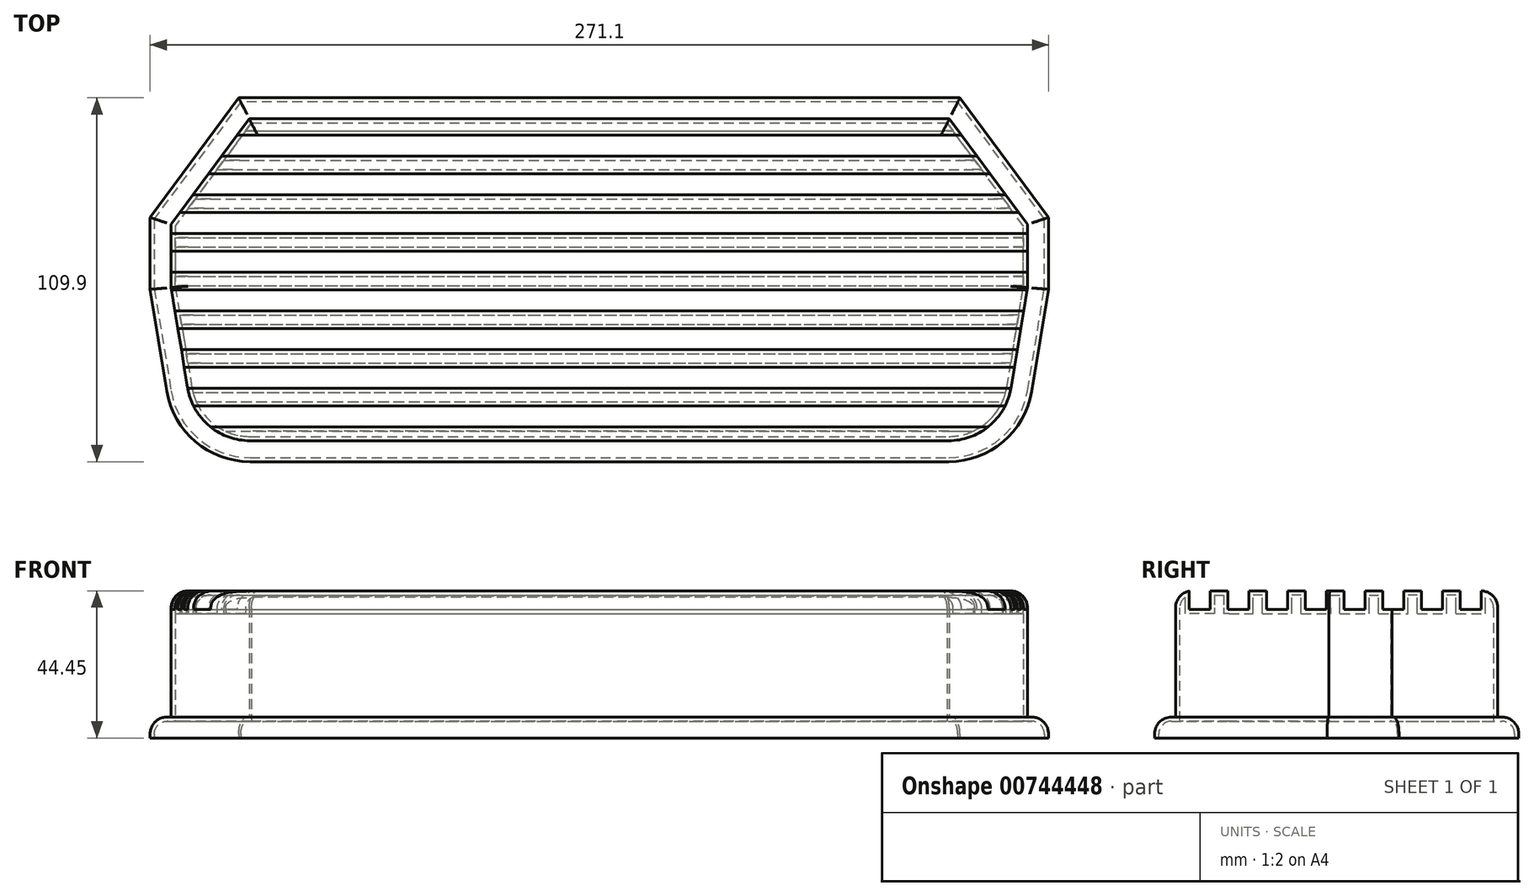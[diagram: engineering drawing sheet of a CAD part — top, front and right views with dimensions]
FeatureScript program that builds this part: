
annotation { "Feature Type Name" : "Feature", "Feature Type Description" : "" }
export const myFeature = defineFeature(function(context is Context, id is Id, definition is map)
    precondition{}
    {
        {
            var Q0;
            Q0=qCreatedBy(makeId("Top.planeOp"),FACE);
            var sketch = newSketch(context, id + "F0", { "sketchPlane" : qUnion([Q0])});
            skLineSegment(sketch, "E0.0.0", {"start": v(-203.12, -79.65) * mm, "end": v(7.7, -79.65) * mm});
            skArc(sketch, "E0.0.1", {"start": v(7.7, -79.65) * mm, "mid": v(20.03, -75.13) * mm, "end": v(26.5, -63.7) * mm});
            skLineSegment(sketch, "E0.0.2", {"start": v(26.5, -63.7) * mm, "end": v(31.49, -33.42) * mm});
            skLineSegment(sketch, "E0.0.3", {"start": v(31.49, -33.42) * mm, "end": v(31.49, -14.33) * mm});
            skLineSegment(sketch, "E0.0.4", {"start": v(31.49, -14.33) * mm, "end": v(7.9, 17.55) * mm});
            skLineSegment(sketch, "E0.0.5", {"start": v(7.9, 17.55) * mm, "end": v(-203.33, 17.55) * mm});
            skLineSegment(sketch, "E0.0.6", {"start": v(-203.33, 17.55) * mm, "end": v(-226.91, -14.33) * mm});
            skLineSegment(sketch, "E0.0.7", {"start": v(-226.91, -14.33) * mm, "end": v(-226.91, -33.42) * mm});
            skLineSegment(sketch, "E0.0.8", {"start": v(-226.91, -33.42) * mm, "end": v(-221.92, -63.7) * mm});
            skArc(sketch, "E0.0.9", {"start": v(-221.92, -63.7) * mm, "mid": v(-215.45, -75.13) * mm, "end": v(-203.12, -79.65) * mm});
            skArc(sketch, "E1.0", {"start": v(-228.19, -64.73) * mm, "mid": v(-219.56, -79.97) * mm, "end": v(-203.12, -86) * mm});
            skLineSegment(sketch, "E1.1", {"start": v(-233.26, -33.94) * mm, "end": v(-228.19, -64.73) * mm});
            skLineSegment(sketch, "E1.2", {"start": v(-203.12, -86) * mm, "end": v(7.7, -86) * mm});
            skLineSegment(sketch, "E1.3", {"start": v(-233.26, -12.24) * mm, "end": v(-233.26, -33.94) * mm});
            skLineSegment(sketch, "E1.4", {"start": v(-206.53, 23.9) * mm, "end": v(-233.26, -12.24) * mm});
            skLineSegment(sketch, "E1.5", {"start": v(11.1, 23.9) * mm, "end": v(-206.53, 23.9) * mm});
            skArc(sketch, "E1.6", {"start": v(7.7, -86) * mm, "mid": v(24.14, -79.97) * mm, "end": v(32.76, -64.73) * mm});
            skLineSegment(sketch, "E1.7", {"start": v(32.76, -64.73) * mm, "end": v(37.84, -33.94) * mm});
            skLineSegment(sketch, "E1.8", {"start": v(37.84, -33.94) * mm, "end": v(37.84, -12.24) * mm});
            skLineSegment(sketch, "E1.9", {"start": v(37.84, -12.24) * mm, "end": v(11.1, 23.9) * mm});
            skSolve(sketch);
        }
        {
            var Q0;
            Q0=makeQuery(id+"F0.imprint","IMPRINT",FACE,{"disambiguationData":[TD([[makeQuery(id+"F0.imprint","IMPRINT",EDGE,{"derivedFrom":sQuery(id+"F0.wireOp",EDGE,"E0.0.0")}),1.0]])]});
            extrude(context, id + "F1", {"entities" : qUnion([Q0]), "depth" : 44.45 * mm});
        }
        {
            var Q0;
            Q0=makeQuery(id+"F0.imprint","IMPRINT",FACE,{"disambiguationData":[TD([[makeQuery(id+"F0.imprint","IMPRINT",EDGE,{"derivedFrom":sQuery(id+"F0.wireOp",EDGE,"E0.0.0")}),-1.0]])]});
            extrude(context, id + "F2", {"entities" : qUnion([Q0]), "operationType" : NewBodyOperationType.ADD, "depth" : 6.35 * mm});
        }
        {
            var Q0;
            Q0=makeQuery(id+"F1.opExtrude","CAP_FACE",FACE,{"disambiguationData":[OSD([sQuery(id+"F0.wireOp",EDGE,"E0.0.0"),sQuery(id+"F0.wireOp",EDGE,"E0.0.1"),sQuery(id+"F0.wireOp",EDGE,"E0.0.2"),sQuery(id+"F0.wireOp",EDGE,"E0.0.3"),sQuery(id+"F0.wireOp",EDGE,"E0.0.4"),sQuery(id+"F0.wireOp",EDGE,"E0.0.5"),sQuery(id+"F0.wireOp",EDGE,"E0.0.6"),sQuery(id+"F0.wireOp",EDGE,"E0.0.7"),sQuery(id+"F0.wireOp",EDGE,"E0.0.8"),sQuery(id+"F0.wireOp",EDGE,"E0.0.9")])],"isStart":false});
            var Q1;
            Q1=makeQuery(id+"F2.opExtrude","CAP_EDGE",EDGE,{"disambiguationData":[OSD([sQuery(id+"F0.wireOp",EDGE,"E1.4")])],"isStart":false});
            var Q2;
            Q2=makeQuery(id+"F2.opExtrude","CAP_EDGE",EDGE,{"disambiguationData":[OSD([sQuery(id+"F0.wireOp",EDGE,"E1.3")])],"isStart":false});
            var Q3;
            Q3=makeQuery(id+"F2.opExtrude","CAP_EDGE",EDGE,{"disambiguationData":[OSD([sQuery(id+"F0.wireOp",EDGE,"E1.1")])],"isStart":false});
            var Q4;
            Q4=makeQuery(id+"F2.opExtrude","CAP_EDGE",EDGE,{"disambiguationData":[OSD([sQuery(id+"F0.wireOp",EDGE,"E1.5")])],"isStart":false});
            var Q5;
            Q5=makeQuery(id+"F2.opExtrude","CAP_EDGE",EDGE,{"disambiguationData":[OSD([sQuery(id+"F0.wireOp",EDGE,"E1.8")])],"isStart":false});
            var Q6;
            Q6=makeQuery(id+"F2.opExtrude","CAP_EDGE",EDGE,{"disambiguationData":[OSD([sQuery(id+"F0.wireOp",EDGE,"E1.9")])],"isStart":false});
            fillet(context, id + "F3", {"entities" : qUnion([Q0, Q1, Q2, Q3, Q4, Q5, Q6]), "radius" : 5.08 * mm, "tangentPropagation" : true, "allowEdgeOverflow" : false});
        }
        {
            var Q0;
            Q0=qCreatedBy(makeId("Right.planeOp"),FACE);
            var sketch = newSketch(context, id + "F4", { "sketchPlane" : qUnion([Q0])});
            skLineSegment(sketch, "E2.bottom", {"start": v(12.62, 51.56) * mm, "end": v(6.27, 51.56) * mm});
            skLineSegment(sketch, "E2.top", {"start": v(12.62, 38.86) * mm, "end": v(6.27, 38.86) * mm});
            skLineSegment(sketch, "E2.left", {"start": v(12.62, 51.56) * mm, "end": v(12.62, 38.86) * mm});
            skLineSegment(sketch, "E2.right", {"start": v(6.27, 51.56) * mm, "end": v(6.27, 38.86) * mm});
            skPoint(sketch, "E2.middle", {"position": v(9.45, 45.2) * mm});
            skLineSegment(sketch, "E3.1.0.0", {"start": v(-5.4, 51.56) * mm, "end": v(-5.4, 38.86) * mm});
            skLineSegment(sketch, "E3.1.0.1", {"start": v(0.94, 51.56) * mm, "end": v(-5.4, 51.56) * mm});
            skLineSegment(sketch, "E3.1.0.2", {"start": v(0.94, 51.56) * mm, "end": v(0.94, 38.86) * mm});
            skLineSegment(sketch, "E3.1.0.3", {"start": v(0.94, 38.86) * mm, "end": v(-5.4, 38.86) * mm});
            skLineSegment(sketch, "E3.2.0.0", {"start": v(-17.1, 51.56) * mm, "end": v(-17.1, 38.86) * mm});
            skLineSegment(sketch, "E3.2.0.1", {"start": v(-10.74, 51.56) * mm, "end": v(-17.1, 51.56) * mm});
            skLineSegment(sketch, "E3.2.0.2", {"start": v(-10.74, 51.56) * mm, "end": v(-10.74, 38.86) * mm});
            skLineSegment(sketch, "E3.2.0.3", {"start": v(-10.74, 38.86) * mm, "end": v(-17.1, 38.86) * mm});
            skLineSegment(sketch, "E3.3.0.0", {"start": v(-28.78, 51.56) * mm, "end": v(-28.78, 38.86) * mm});
            skLineSegment(sketch, "E3.3.0.1", {"start": v(-22.43, 51.56) * mm, "end": v(-28.78, 51.56) * mm});
            skLineSegment(sketch, "E3.3.0.2", {"start": v(-22.43, 51.56) * mm, "end": v(-22.43, 38.86) * mm});
            skLineSegment(sketch, "E3.3.0.3", {"start": v(-22.43, 38.86) * mm, "end": v(-28.78, 38.86) * mm});
            skLineSegment(sketch, "E3.4.0.0", {"start": v(-40.46, 51.56) * mm, "end": v(-40.46, 38.86) * mm});
            skLineSegment(sketch, "E3.4.0.1", {"start": v(-34.11, 51.56) * mm, "end": v(-40.46, 51.56) * mm});
            skLineSegment(sketch, "E3.4.0.2", {"start": v(-34.11, 51.56) * mm, "end": v(-34.11, 38.86) * mm});
            skLineSegment(sketch, "E3.4.0.3", {"start": v(-34.11, 38.86) * mm, "end": v(-40.46, 38.86) * mm});
            skLineSegment(sketch, "E3.5.0.0", {"start": v(-52.15, 51.56) * mm, "end": v(-52.15, 38.86) * mm});
            skLineSegment(sketch, "E3.5.0.1", {"start": v(-45.8, 51.56) * mm, "end": v(-52.15, 51.56) * mm});
            skLineSegment(sketch, "E3.5.0.2", {"start": v(-45.8, 51.56) * mm, "end": v(-45.8, 38.86) * mm});
            skLineSegment(sketch, "E3.5.0.3", {"start": v(-45.8, 38.86) * mm, "end": v(-52.15, 38.86) * mm});
            skLineSegment(sketch, "E3.6.0.0", {"start": v(-63.83, 51.56) * mm, "end": v(-63.83, 38.86) * mm});
            skLineSegment(sketch, "E3.6.0.1", {"start": v(-57.48, 51.56) * mm, "end": v(-63.83, 51.56) * mm});
            skLineSegment(sketch, "E3.6.0.2", {"start": v(-57.48, 51.56) * mm, "end": v(-57.48, 38.86) * mm});
            skLineSegment(sketch, "E3.6.0.3", {"start": v(-57.48, 38.86) * mm, "end": v(-63.83, 38.86) * mm});
            skLineSegment(sketch, "E3.7.0.0", {"start": v(-75.51, 51.56) * mm, "end": v(-75.51, 38.86) * mm});
            skLineSegment(sketch, "E3.7.0.1", {"start": v(-69.16, 51.56) * mm, "end": v(-75.51, 51.56) * mm});
            skLineSegment(sketch, "E3.7.0.2", {"start": v(-69.16, 51.56) * mm, "end": v(-69.16, 38.86) * mm});
            skLineSegment(sketch, "E3.7.0.3", {"start": v(-69.16, 38.86) * mm, "end": v(-75.51, 38.86) * mm});
            skLineSegment(sketch, "E3.direction1", {"start": v(6.27, 38.86) * mm, "end": v(-5.4, 38.86) * mm, "construction": true});
            skSolve(sketch);
        }
        {
            var Q0;
            Q0=makeQuery(id+"F4.imprint","IMPRINT",FACE,{"disambiguationData":[TD([[makeQuery(id+"F4.imprint","IMPRINT",EDGE,{"derivedFrom":sQuery(id+"F4.wireOp",EDGE,"E2.bottom")}),1.0]])]});
            var Q1;
            Q1=makeQuery(id+"F4.imprint","IMPRINT",FACE,{"disambiguationData":[TD([[makeQuery(id+"F4.imprint","IMPRINT",EDGE,{"derivedFrom":sQuery(id+"F4.wireOp",EDGE,"E3.1.0.0")}),1.0]])]});
            var Q2;
            Q2=makeQuery(id+"F4.imprint","IMPRINT",FACE,{"disambiguationData":[TD([[makeQuery(id+"F4.imprint","IMPRINT",EDGE,{"derivedFrom":sQuery(id+"F4.wireOp",EDGE,"E3.2.0.0")}),1.0]])]});
            var Q3;
            Q3=makeQuery(id+"F4.imprint","IMPRINT",FACE,{"disambiguationData":[TD([[makeQuery(id+"F4.imprint","IMPRINT",EDGE,{"derivedFrom":sQuery(id+"F4.wireOp",EDGE,"E3.3.0.0")}),1.0]])]});
            var Q4;
            Q4=makeQuery(id+"F4.imprint","IMPRINT",FACE,{"disambiguationData":[TD([[makeQuery(id+"F4.imprint","IMPRINT",EDGE,{"derivedFrom":sQuery(id+"F4.wireOp",EDGE,"E3.4.0.0")}),1.0]])]});
            var Q5;
            Q5=makeQuery(id+"F4.imprint","IMPRINT",FACE,{"disambiguationData":[TD([[makeQuery(id+"F4.imprint","IMPRINT",EDGE,{"derivedFrom":sQuery(id+"F4.wireOp",EDGE,"E3.5.0.0")}),1.0]])]});
            var Q6;
            Q6=makeQuery(id+"F4.imprint","IMPRINT",FACE,{"disambiguationData":[TD([[makeQuery(id+"F4.imprint","IMPRINT",EDGE,{"derivedFrom":sQuery(id+"F4.wireOp",EDGE,"E3.6.0.0")}),1.0]])]});
            var Q7;
            Q7=makeQuery(id+"F4.imprint","IMPRINT",FACE,{"disambiguationData":[TD([[makeQuery(id+"F4.imprint","IMPRINT",EDGE,{"derivedFrom":sQuery(id+"F4.wireOp",EDGE,"E3.7.0.0")}),1.0]])]});
            extrude(context, id + "F5", {"entities" : qUnion([Q0, Q1, Q2, Q3, Q4, Q5, Q6, Q7]), "operationType" : NewBodyOperationType.REMOVE, "endBound" : BoundingType.SYMMETRIC, "oppositeDirection" : true, "depth" : 762 * mm});
        }
        {
            var Q0;
            {var subQ0=sQuery(id+"F0.wireOp",EDGE,"E0.0.9");var subQ1=sQuery(id+"F0.wireOp",EDGE,"E0.0.8");var subQ2=sQuery(id+"F0.wireOp",EDGE,"E0.0.7");var subQ3=sQuery(id+"F0.wireOp",EDGE,"E0.0.6");var subQ4=sQuery(id+"F0.wireOp",EDGE,"E0.0.5");var subQ5=sQuery(id+"F0.wireOp",EDGE,"E0.0.4");var subQ6=sQuery(id+"F0.wireOp",EDGE,"E0.0.3");var subQ7=sQuery(id+"F0.wireOp",EDGE,"E0.0.2");var subQ8=sQuery(id+"F0.wireOp",EDGE,"E0.0.1");var subQ9=sQuery(id+"F0.wireOp",EDGE,"E0.0.0");Q0=makeQuery(id+"F2.boolean.opBoolean","MERGE",FACE,{"derivedFrom":[makeQuery(id+"F1.opExtrude","CAP_FACE",FACE,{"disambiguationData":[OSD([subQ9,subQ8,subQ7,subQ6,subQ5,subQ4,subQ3,subQ2,subQ1,subQ0])],"isStart":true}),makeQuery(id+"F2.opExtrude","CAP_FACE",FACE,{"disambiguationData":[OSD([subQ9,subQ8,subQ7,subQ6,subQ5,subQ4,subQ3,subQ2,subQ1,subQ0,sQuery(id+"F0.wireOp",EDGE,"E1.0"),sQuery(id+"F0.wireOp",EDGE,"E1.1"),sQuery(id+"F0.wireOp",EDGE,"E1.2"),sQuery(id+"F0.wireOp",EDGE,"E1.3"),sQuery(id+"F0.wireOp",EDGE,"E1.4"),sQuery(id+"F0.wireOp",EDGE,"E1.5"),sQuery(id+"F0.wireOp",EDGE,"E1.6"),sQuery(id+"F0.wireOp",EDGE,"E1.7"),sQuery(id+"F0.wireOp",EDGE,"E1.8"),sQuery(id+"F0.wireOp",EDGE,"E1.9")])],"isStart":true})]});}
            shell(context, id + "F6", {"entities" : qUnion([Q0]), "thickness" : 1.27 * mm});
        }
    });
